# Revit family: Grohe_HandShower_EuphoriaCosmopolitan_22126KF0
name_source: partatom
category: Plumbing Fixtures
units: mm (PartAtom-declared; Revit-internal decimal feet)

## family parameters
Cut with Voids When Loaded = No
Host = Face
OmniClass Number = 23.45.05.00
OmniClass Title = Sanitary Equipment
Part Type = Normal
Room Calculation Point = No
Round Connector Dimension = Use Diameter
Shared = No

## types (1)
- EUPHORIA COSMOPOLITAN Hand Shower (22126KF0)
    Assembly Code = D2010
    AssetType = Fixed
    BIMObjectName = Grohe_HandShower_EuphoriaCosmopolitan_22126KF0
    CO2NeutralProduction = GROHE is one of the first leading manufacturer within the sanitary industry having a CO2-neutral production.
    CW Connection = No
    ClassificationName = Uniclass2015
    ClassificationValue = Pr_40_20_87_76
    Color = Matt Black
    Cost = 0 $
    Default Elevation = 0 mm  [stored 0 ft]
    Description = EUPHORIA COSMOPOLITAN Hand Shower
    DimensionsDocumentLink = https://cdn.cloud.grohe.com
    DocumentationCertificates = https://www.bimstore.co
    DocumentationInstallationGuide = https://www.bimstore.co
    DocumentationLiterature = https://www.bimstore.co
    DocumentationMaintenance = https://www.bimstore.co
    DocumentationTechnical = https://www.bimstore.co
    DurationUnit = Years
    EF000653 = TRUE
    EF001707 = 70 °C
    EF002169 = Plastic
    EF002616 = FALSE
    EF002671 = Other
    EF015313 = not applicable
    EF021038 = 8.00
    EF021039 = TRUE
    EF021040 = 1
    EF021041 = 0
    EF021042 = FALSE
    EF022042 = Z
    EF022224 = FALSE
    EF022337 = FALSE
    EF023440 = FALSE
    EF023686 = not applicable
    EF024050 = FALSE
    EF025080 = TRUE
    EF025094 = 0
    Ecojoy = No
    ExpectedLife = 0
    FullRecyclabilityOfPlastic = All plastic components are fully recyclable
    GROHESocialCommittment = green.grohe.com/social_engagement
    GROHESustainability = green.grohe.com
    HW Connection = No
    IfcExportAs = IfcPipeFitting
    IfcExportType = IfcPipeFittingType
    Keynote = N13
    Manufacturer = Grohe
    ManufacturerName = Grohe
    Model = EUPHORIA COSMOPOLITAN Hand Shower
    ModelNumber = 22126KF0
    ModelReference = EUPHORIA COSMOPOLITAN Hand Shower
    NBSDescription = Shower heads
    NBSObjectName = Grohe - Shower heads
    NBSReference = 45-35-70/333
    NominalDepth = 0 mm  [stored 0 ft]
    NominalHeight = 0 mm  [stored 0 ft]
    NominalLength = 0 mm  [stored 0 ft]
    PQDiagramLink = https://cdn.cloud.grohe.com
    PrimaryMaterial = Grohe_MattBlack
    ProductDescription = Normal spray

GROHE Water Saving 9.5 l/min flow limiter

GROHE Long-Life Shine finish

SpeedClean anti-limescale system

Inner WaterGuide for a longer life

universal mounting system, fitting all standard shower hoses

suitable for instantaneous heater

min. recommended pressure 1.0 bar
    ProductNumber = 22126KF0
    ProductPageURL = https://www.grohe.co.uk
    ProductShortText = Euphoria Cosmopolitan Hand shower 1 spray
    ProductType = Single Shower
    ProductionYear = 2023
    SustainabilityAward = green.grohe.com/awards
    SustainabilityReport = green.grohe.com/reporting
    Type Comments = EUPHORIA COSMOPOLITAN Hand Shower
    TypeName = EUPHORIA COSMOPOLITAN Hand Shower
    URL = https://www.grohe.co.uk
    Vent Connection = No
    WarrantyDurationLabor = 0
    WarrantyDurationParts = 0
    WarrantyDurationUnit = Years
    Waste Connection = No
    _BSBibleVersion = 17
    _BimSpecGuid = 0
    _CurrentRevision = 1
    _DistributedBy = https://www.bimstore.co
    _ObjectUserGuide = https://www.bimstore.co

note: [stored X ft] marks values corroborated as IEEE doubles in the binary element streams (Revit-internal decimal feet)

## geometry (parser evidence)
native form markers: Sweep x2
no freeform markers — native parametric forms only
